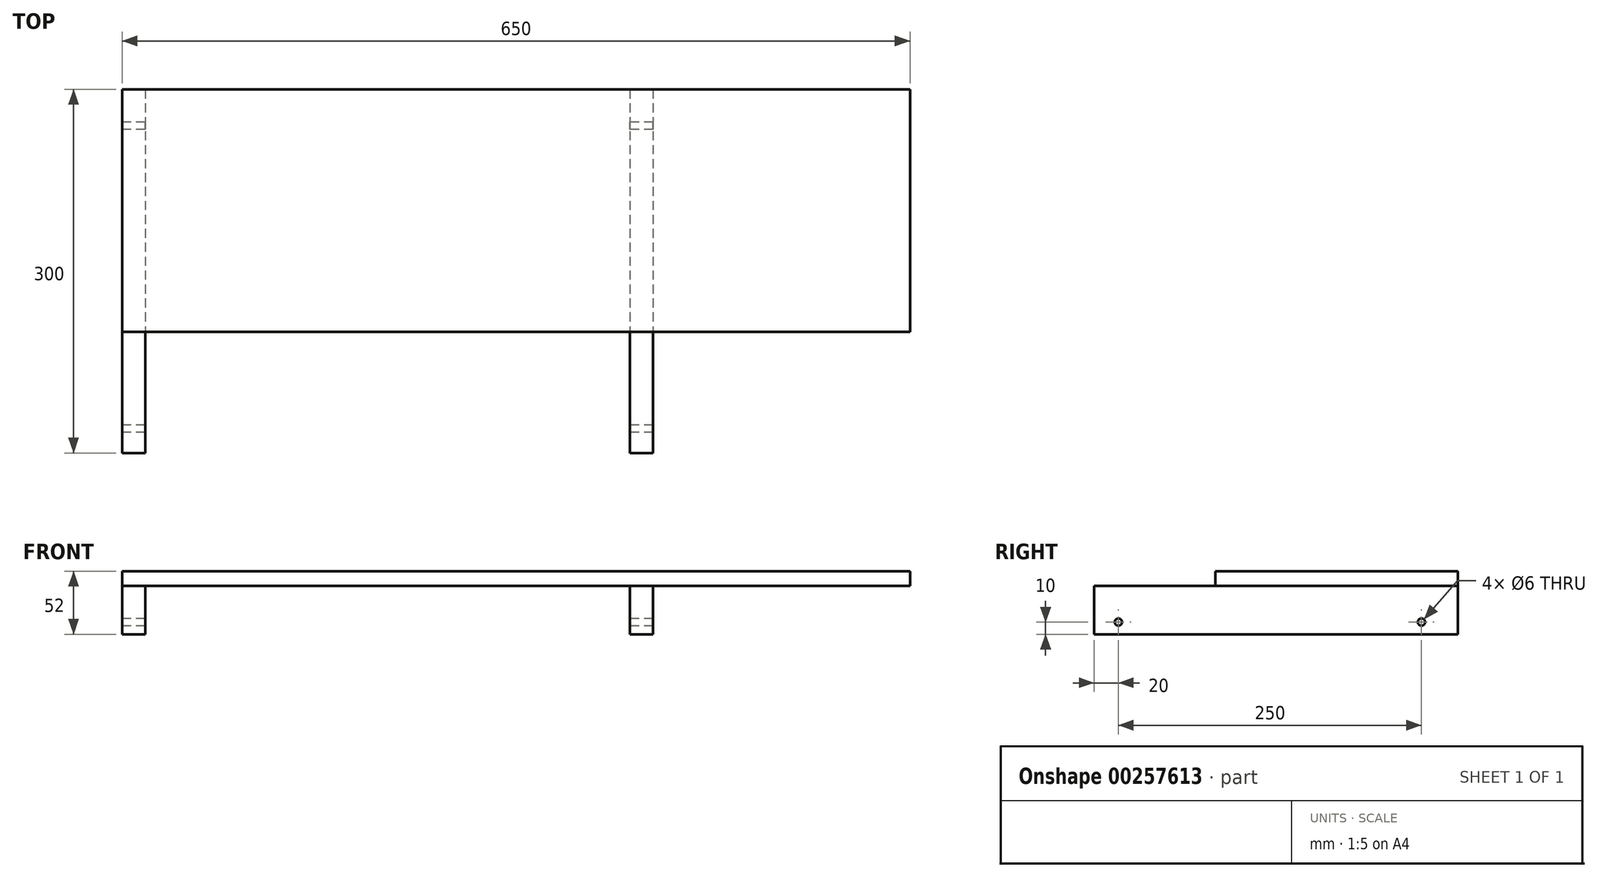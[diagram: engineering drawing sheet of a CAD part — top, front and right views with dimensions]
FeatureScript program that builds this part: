
annotation { "Feature Type Name" : "Feature", "Feature Type Description" : "" }
export const myFeature = defineFeature(function(context is Context, id is Id, definition is map)
    precondition{}
    {
        {
            var Q0;
            Q0=qCreatedBy(makeId("Top.planeOp"),FACE);
            var sketch = newSketch(context, id + "F0", { "sketchPlane" : qUnion([Q0])});
            skLineSegment(sketch, "E0.bottom", {"start": v(0, 0) * mm, "end": v(650, 0) * mm});
            skLineSegment(sketch, "E0.top", {"start": v(0, 200) * mm, "end": v(650, 200) * mm});
            skLineSegment(sketch, "E0.left", {"start": v(0, 0) * mm, "end": v(0, 200) * mm});
            skLineSegment(sketch, "E0.right", {"start": v(650, 0) * mm, "end": v(650, 200) * mm});
            skSolve(sketch);
        }
        {
            var Q0;
            Q0 = qSketchRegion(id + "F0", true);
            extrude(context, id + "F1", {"entities" : qUnion([Q0]), "depth" : 12 * mm});
        }
        {
            var Q0;
            Q0=qCreatedBy(makeId("Front.planeOp"),FACE);
            var sketch = newSketch(context, id + "F2", { "sketchPlane" : qUnion([Q0])});
            skLineSegment(sketch, "E1.bottom", {"start": v(0, 0) * mm, "end": v(19, 0) * mm});
            skLineSegment(sketch, "E1.top", {"start": v(0, -40) * mm, "end": v(19, -40) * mm});
            skLineSegment(sketch, "E1.left", {"start": v(0, 0) * mm, "end": v(0, -40) * mm});
            skLineSegment(sketch, "E1.right", {"start": v(19, 0) * mm, "end": v(19, -40) * mm});
            skLineSegment(sketch, "E2.bottom", {"start": v(419, 0) * mm, "end": v(438, 0) * mm});
            skLineSegment(sketch, "E2.top", {"start": v(419, -40) * mm, "end": v(438, -40) * mm});
            skLineSegment(sketch, "E2.left", {"start": v(419, 0) * mm, "end": v(419, -40) * mm});
            skLineSegment(sketch, "E2.right", {"start": v(438, 0) * mm, "end": v(438, -40) * mm});
            skSolve(sketch);
        }
        {
            var Q0;
            Q0 = qSketchRegion(id + "F2", true);
            var Q1;
            Q1=makeQuery(id+"F1.opExtrude","SWEPT_FACE",FACE,{"disambiguationData":[OSD([sQuery(id+"F0.wireOp",EDGE,"E0.top")])]});
            extrude(context, id + "F3", {"entities" : qUnion([Q0]), "operationType" : NewBodyOperationType.ADD, "endBound" : BoundingType.UP_TO_SURFACE, "oppositeDirection" : true, "endBoundEntityFace" : qUnion([Q1]), "depth" : 25 * mm, "hasSecondDirection" : true, "secondDirectionOppositeDirection" : false, "secondDirectionDepth" : 100 * mm});
        }
        {
            var Q0;
            Q0=makeQuery(id+"F3.boolean.opBoolean","MERGE",FACE,{"derivedFrom":[makeQuery(id+"F1.opExtrude","SWEPT_FACE",FACE,{"disambiguationData":[OSD([sQuery(id+"F0.wireOp",EDGE,"E0.left")])]}),makeQuery(id+"F3.opExtrude","SWEPT_FACE",FACE,{"disambiguationData":[OSD([sQuery(id+"F2.wireOp",EDGE,"E1.left")])]})]});
            var sketch = newSketch(context, id + "F4", { "sketchPlane" : qUnion([Q0])});
            skCircle(sketch, "E3", {"center": v(80, -30) * mm, "radius": 3 * mm});
            skCircle(sketch, "E4", {"center": v(-170, -30) * mm, "radius": 3 * mm});
            skSolve(sketch);
        }
        {
            var Q0;
            Q0 = qSketchRegion(id + "F4", true);
            extrude(context, id + "F5", {"entities" : qUnion([Q0]), "operationType" : NewBodyOperationType.REMOVE, "endBound" : BoundingType.THROUGH_ALL, "oppositeDirection" : true, "depth" : 25 * mm});
        }
    });
